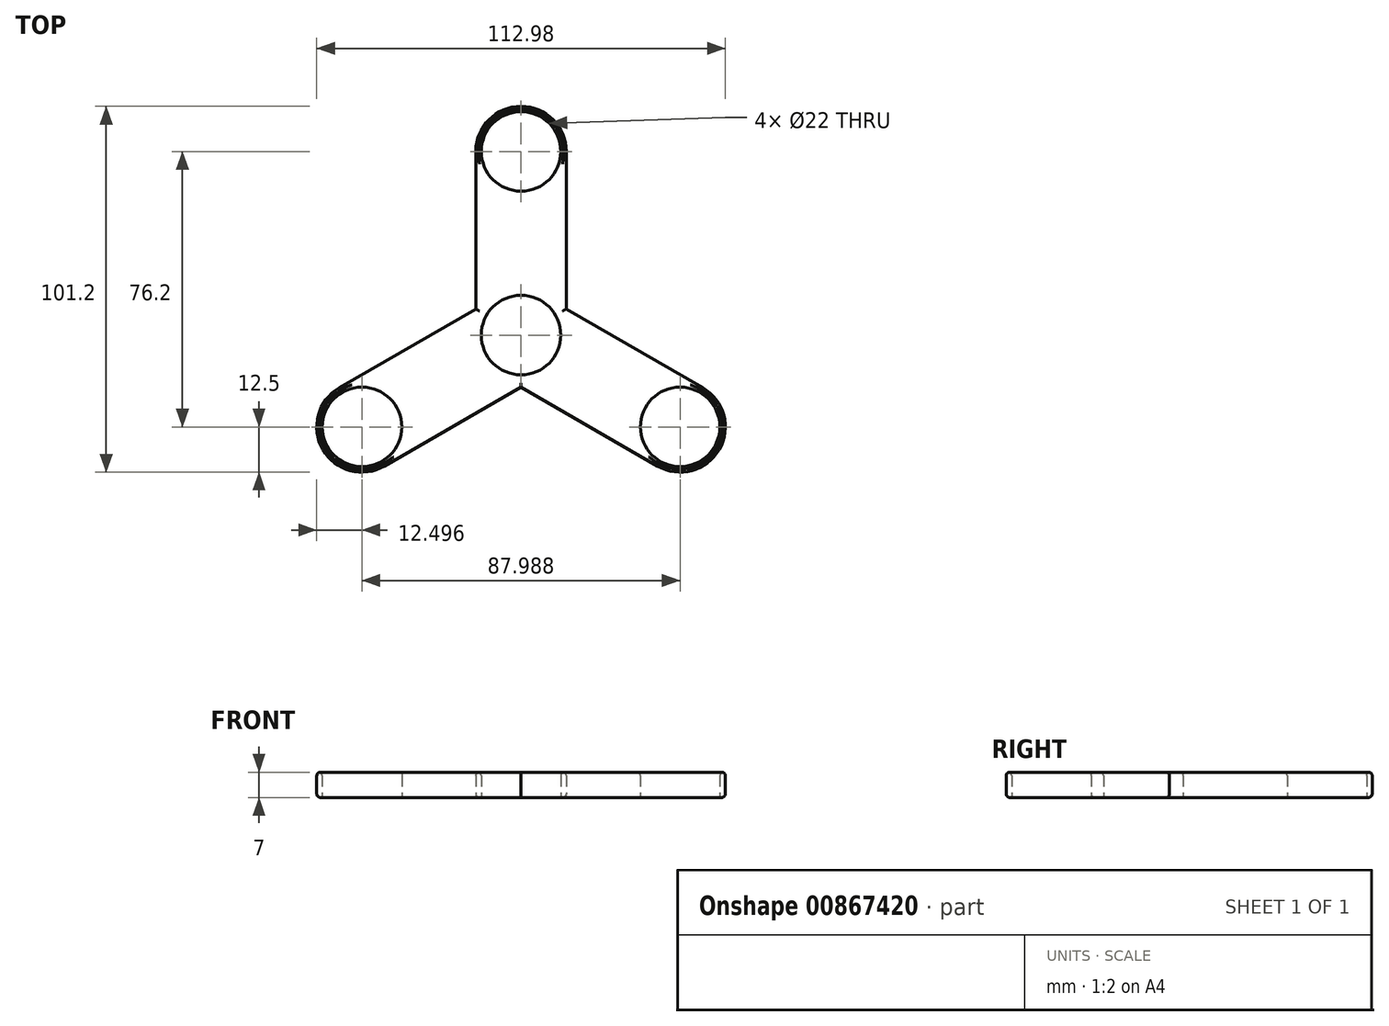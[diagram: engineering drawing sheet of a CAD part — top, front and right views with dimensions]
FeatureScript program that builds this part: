
annotation { "Feature Type Name" : "Feature", "Feature Type Description" : "" }
export const myFeature = defineFeature(function(context is Context, id is Id, definition is map)
    precondition{}
    {
        {
            var Q0;
            Q0=qCreatedBy(makeId("Top.planeOp"),FACE);
            var sketch = newSketch(context, id + "F0", { "sketchPlane" : qUnion([Q0])});
            skLineSegment(sketch, "E0", {"start": v(-12.5, 50.8) * mm, "end": v(-12.5, 7.22) * mm});
            skLineSegment(sketch, "E1", {"start": v(12.5, 50.8) * mm, "end": v(12.5, 0) * mm});
            skArc(sketch, "E2", {"start": v(12.5, 50.8) * mm, "mid": v(0, 63.3) * mm, "end": v(-12.5, 50.8) * mm});
            skLineSegment(sketch, "E3.1.0", {"start": v(-37.74, -36.23) * mm, "end": v(0, -14.43) * mm});
            skArc(sketch, "E3.1.1", {"start": v(-50.24, -14.57) * mm, "mid": v(-54.82, -31.65) * mm, "end": v(-37.74, -36.23) * mm});
            skLineSegment(sketch, "E3.1.2", {"start": v(-50.24, -14.57) * mm, "end": v(-12.5, 7.22) * mm});
            skLineSegment(sketch, "E3.2.0", {"start": v(50.24, -14.57) * mm, "end": v(12.5, 7.22) * mm});
            skArc(sketch, "E3.2.1", {"start": v(37.74, -36.23) * mm, "mid": v(54.82, -31.65) * mm, "end": v(50.24, -14.57) * mm});
            skLineSegment(sketch, "E3.2.2", {"start": v(37.74, -36.23) * mm, "end": v(0, -14.43) * mm});
            skPoint(sketch, "E3.center", {"position": v(0, 0) * mm});
            skPoint(sketch, "E4.orphan", {"position": v(-6.25, 10.83) * mm});
            skPoint(sketch, "E5.orphan", {"position": v(-12.5, 0) * mm});
            skPoint(sketch, "E6.orphan", {"position": v(6.25, 10.83) * mm});
            skPoint(sketch, "E7.orphan", {"position": v(6.25, -10.83) * mm});
            skPoint(sketch, "E8.orphan", {"position": v(-6.25, -10.83) * mm});
            skSolve(sketch);
        }
        {
            var Q0;
            Q0=qCreatedBy(makeId("Top.planeOp"),FACE);
            var sketch = newSketch(context, id + "F1", { "sketchPlane" : qUnion([Q0])});
            skCircle(sketch, "E9", {"center": v(0, 50.8) * mm, "radius": 11 * mm});
            skCircle(sketch, "E10.1.0", {"center": v(-44, -25.4) * mm, "radius": 11 * mm});
            skCircle(sketch, "E10.2.0", {"center": v(44, -25.4) * mm, "radius": 11 * mm});
            skPoint(sketch, "E10.center", {"position": v(0, 0) * mm});
            skCircle(sketch, "E11", {"center": v(0, 0) * mm, "radius": 11 * mm});
            skSolve(sketch);
        }
        {
            var Q0;
            Q0 = qSketchRegion(id + "F0", true);
            extrude(context, id + "F2", {"entities" : qUnion([Q0]), "depth" : 7 * mm, "offsetDistance" : 25.4 * mm});
        }
        {
            var Q0;
            Q0 = qSketchRegion(id + "F1", true);
            extrude(context, id + "F3", {"entities" : qUnion([Q0]), "operationType" : NewBodyOperationType.REMOVE, "depth" : 25.4 * mm, "offsetDistance" : 25.4 * mm});
        }
        {
            var Q0;
            Q0=makeQuery(id+"F3.boolean.opBoolean","INTERSECT",EDGE,{"derivedFrom":[makeQuery(id+"F2.opExtrude","CAP_FACE",FACE,{"disambiguationData":[OSD([sQuery(id+"F0.wireOp",EDGE,"E0"),sQuery(id+"F0.wireOp",EDGE,"E1"),sQuery(id+"F0.wireOp",EDGE,"E2"),sQuery(id+"F0.wireOp",EDGE,"E3.1.0"),sQuery(id+"F0.wireOp",EDGE,"E3.1.1"),sQuery(id+"F0.wireOp",EDGE,"E3.1.2"),sQuery(id+"F0.wireOp",EDGE,"E3.2.0"),sQuery(id+"F0.wireOp",EDGE,"E3.2.1"),sQuery(id+"F0.wireOp",EDGE,"E3.2.2")])],"isStart":false}),makeQuery(id+"F3.opExtrude","SWEPT_FACE",FACE,{"disambiguationData":[OSD([sQuery(id+"F1.wireOp",EDGE,"E9")])]})]});
            var Q1;
            Q1=makeQuery(id+"F3.boolean.opBoolean","COPY",EDGE,{"derivedFrom":makeQuery(id+"F3.opExtrude","CAP_EDGE",EDGE,{"disambiguationData":[OSD([sQuery(id+"F1.wireOp",EDGE,"E9")])],"isStart":true})});
            var Q2;
            Q2=makeQuery(id+"F2.opExtrude","CAP_EDGE",EDGE,{"disambiguationData":[OSD([sQuery(id+"F0.wireOp",EDGE,"E0")])],"isStart":true});
            var Q3;
            Q3=makeQuery(id+"F2.opExtrude","CAP_EDGE",EDGE,{"disambiguationData":[OSD([sQuery(id+"F0.wireOp",EDGE,"E1")])],"isStart":true});
            var Q4;
            Q4=makeQuery(id+"F2.opExtrude","CAP_EDGE",EDGE,{"disambiguationData":[OSD([sQuery(id+"F0.wireOp",EDGE,"E1")])],"isStart":false});
            var Q5;
            Q5=makeQuery(id+"F2.opExtrude","CAP_EDGE",EDGE,{"disambiguationData":[OSD([sQuery(id+"F0.wireOp",EDGE,"E3.1.2")])],"isStart":true});
            var Q6;
            Q6=makeQuery(id+"F2.opExtrude","CAP_EDGE",EDGE,{"disambiguationData":[OSD([sQuery(id+"F0.wireOp",EDGE,"E3.1.2")])],"isStart":false});
            var Q7;
            Q7=makeQuery(id+"F3.boolean.opBoolean","COPY",EDGE,{"derivedFrom":makeQuery(id+"F3.opExtrude","CAP_EDGE",EDGE,{"disambiguationData":[OSD([sQuery(id+"F1.wireOp",EDGE,"E10.1.0")])],"isStart":true})});
            var Q8;
            Q8=makeQuery(id+"F3.boolean.opBoolean","INTERSECT",EDGE,{"derivedFrom":[makeQuery(id+"F2.opExtrude","CAP_FACE",FACE,{"disambiguationData":[OSD([sQuery(id+"F0.wireOp",EDGE,"E0"),sQuery(id+"F0.wireOp",EDGE,"E1"),sQuery(id+"F0.wireOp",EDGE,"E2"),sQuery(id+"F0.wireOp",EDGE,"E3.1.0"),sQuery(id+"F0.wireOp",EDGE,"E3.1.1"),sQuery(id+"F0.wireOp",EDGE,"E3.1.2"),sQuery(id+"F0.wireOp",EDGE,"E3.2.0"),sQuery(id+"F0.wireOp",EDGE,"E3.2.1"),sQuery(id+"F0.wireOp",EDGE,"E3.2.2")])],"isStart":false}),makeQuery(id+"F3.opExtrude","SWEPT_FACE",FACE,{"disambiguationData":[OSD([sQuery(id+"F1.wireOp",EDGE,"E10.1.0")])]})]});
            var Q9;
            Q9=makeQuery(id+"F2.opExtrude","CAP_EDGE",EDGE,{"disambiguationData":[OSD([sQuery(id+"F0.wireOp",EDGE,"E3.2.0")])],"isStart":false});
            var Q10;
            Q10=makeQuery(id+"F2.opExtrude","CAP_EDGE",EDGE,{"disambiguationData":[OSD([sQuery(id+"F0.wireOp",EDGE,"E3.2.2")])],"isStart":false});
            var Q11;
            Q11=makeQuery(id+"F3.boolean.opBoolean","INTERSECT",EDGE,{"derivedFrom":[makeQuery(id+"F2.opExtrude","CAP_FACE",FACE,{"disambiguationData":[OSD([sQuery(id+"F0.wireOp",EDGE,"E0"),sQuery(id+"F0.wireOp",EDGE,"E1"),sQuery(id+"F0.wireOp",EDGE,"E2"),sQuery(id+"F0.wireOp",EDGE,"E3.1.0"),sQuery(id+"F0.wireOp",EDGE,"E3.1.1"),sQuery(id+"F0.wireOp",EDGE,"E3.1.2"),sQuery(id+"F0.wireOp",EDGE,"E3.2.0"),sQuery(id+"F0.wireOp",EDGE,"E3.2.1"),sQuery(id+"F0.wireOp",EDGE,"E3.2.2")])],"isStart":false}),makeQuery(id+"F3.opExtrude","SWEPT_FACE",FACE,{"disambiguationData":[OSD([sQuery(id+"F1.wireOp",EDGE,"E10.2.0")])]})]});
            var Q12;
            Q12=makeQuery(id+"F3.boolean.opBoolean","COPY",EDGE,{"derivedFrom":makeQuery(id+"F3.opExtrude","CAP_EDGE",EDGE,{"disambiguationData":[OSD([sQuery(id+"F1.wireOp",EDGE,"E10.2.0")])],"isStart":true})});
            var Q13;
            Q13=makeQuery(id+"F2.opExtrude","CAP_EDGE",EDGE,{"disambiguationData":[OSD([sQuery(id+"F0.wireOp",EDGE,"E3.2.2")])],"isStart":true});
            var Q14;
            Q14=makeQuery(id+"F2.opExtrude","CAP_EDGE",EDGE,{"disambiguationData":[OSD([sQuery(id+"F0.wireOp",EDGE,"E3.2.0")])],"isStart":true});
            fillet(context, id + "F4", {"entities" : qUnion([Q0, Q1, Q2, Q3, Q4, Q5, Q6, Q7, Q8, Q9, Q10, Q11, Q12, Q13, Q14]), "radius" : 1 * mm, "tangentPropagation" : true, "allowEdgeOverflow" : false});
        }
        {
            var Q0;
            Q0=makeQuery(id+"F3.boolean.opBoolean","INTERSECT",EDGE,{"derivedFrom":[makeQuery(id+"F2.opExtrude","CAP_FACE",FACE,{"disambiguationData":[OSD([sQuery(id+"F0.wireOp",EDGE,"E0"),sQuery(id+"F0.wireOp",EDGE,"E1"),sQuery(id+"F0.wireOp",EDGE,"E2"),sQuery(id+"F0.wireOp",EDGE,"E3.1.0"),sQuery(id+"F0.wireOp",EDGE,"E3.1.1"),sQuery(id+"F0.wireOp",EDGE,"E3.1.2"),sQuery(id+"F0.wireOp",EDGE,"E3.2.0"),sQuery(id+"F0.wireOp",EDGE,"E3.2.1"),sQuery(id+"F0.wireOp",EDGE,"E3.2.2")])],"isStart":false}),makeQuery(id+"F3.opExtrude","SWEPT_FACE",FACE,{"disambiguationData":[OSD([sQuery(id+"F1.wireOp",EDGE,"E11")])]})]});
            var Q1;
            Q1=makeQuery(id+"F3.boolean.opBoolean","COPY",EDGE,{"derivedFrom":makeQuery(id+"F3.opExtrude","CAP_EDGE",EDGE,{"disambiguationData":[OSD([sQuery(id+"F1.wireOp",EDGE,"E11")])],"isStart":true})});
            fillet(context, id + "F5", {"entities" : qUnion([Q0, Q1]), "radius" : 1 * mm, "tangentPropagation" : true, "allowEdgeOverflow" : false});
        }
    });
